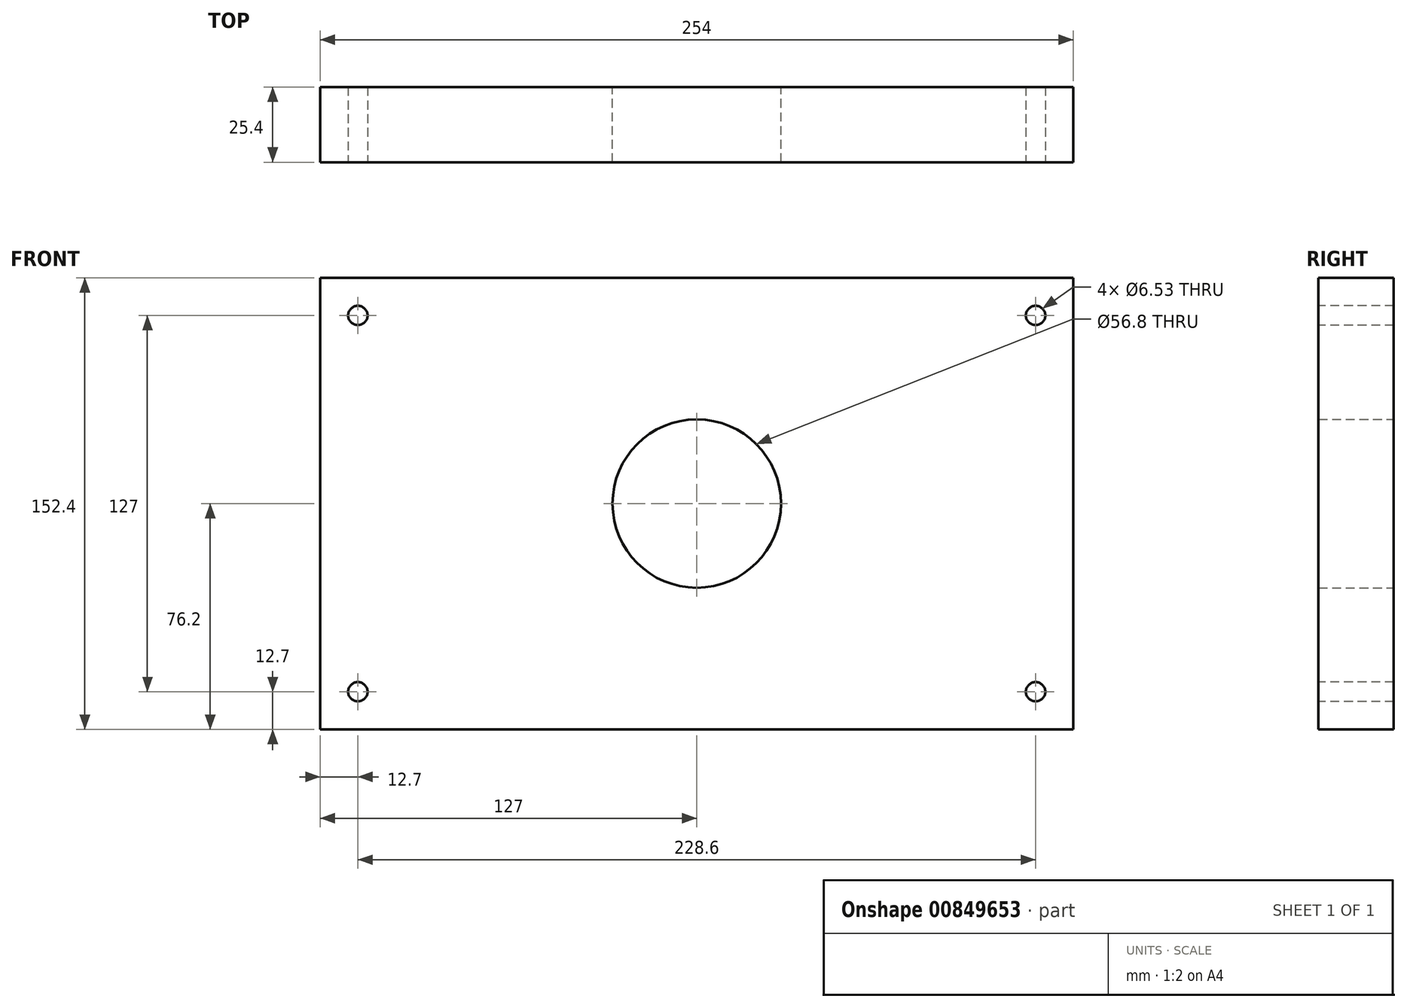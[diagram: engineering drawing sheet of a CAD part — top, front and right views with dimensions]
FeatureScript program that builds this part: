
annotation { "Feature Type Name" : "Feature", "Feature Type Description" : "" }
export const myFeature = defineFeature(function(context is Context, id is Id, definition is map)
    precondition{}
    {
        {
            var Q0;
            Q0=qCreatedBy(makeId("Front.planeOp"),FACE);
            var sketch = newSketch(context, id + "F0", { "sketchPlane" : qUnion([Q0])});
            skLineSegment(sketch, "E0", {"start": v(0, 0) * mm, "end": v(254, 0) * mm});
            skLineSegment(sketch, "E1", {"start": v(254, 0) * mm, "end": v(254, 152.4) * mm});
            skLineSegment(sketch, "E2", {"start": v(254, 152.4) * mm, "end": v(0, 152.4) * mm});
            skLineSegment(sketch, "E3", {"start": v(0, 152.4) * mm, "end": v(0, 0) * mm});
            skSolve(sketch);
        }
        {
            var Q0;
            Q0=makeQuery(id+"F0.imprint","IMPRINT",FACE,{"disambiguationData":[TD([[makeQuery(id+"F0.imprint","IMPRINT",EDGE,{"derivedFrom":sQuery(id+"F0.wireOp",EDGE,"E0")}),1.0]])]});
            extrude(context, id + "F1", {"entities" : qUnion([Q0]), "depth" : 25.4 * mm, "offsetDistance" : 25.4 * mm});
        }
        {
            var Q0;
            Q0=makeQuery(id+"F1.opExtrude","CAP_FACE",FACE,{"disambiguationData":[OSD([sQuery(id+"F0.wireOp",EDGE,"E0"),sQuery(id+"F0.wireOp",EDGE,"E1"),sQuery(id+"F0.wireOp",EDGE,"E2"),sQuery(id+"F0.wireOp",EDGE,"E3")])],"isStart":false});
            var sketch = newSketch(context, id + "F2", { "sketchPlane" : qUnion([Q0])});
            skPoint(sketch, "E4", {"position": v(12.7, 139.7) * mm});
            skPoint(sketch, "E5", {"position": v(241.3, 139.7) * mm});
            skPoint(sketch, "E6", {"position": v(241.3, 12.7) * mm});
            skPoint(sketch, "E7", {"position": v(12.7, 12.7) * mm});
            skSolve(sketch);
        }
        {
            var Q0;
            Q0=sQuery(id+"F2.wireOp",VERTEX,"E4");
            var Q1;
            Q1=sQuery(id+"F2.wireOp",VERTEX,"E5");
            var Q2;
            Q2=sQuery(id+"F2.wireOp",VERTEX,"E6");
            var Q3;
            Q3=sQuery(id+"F2.wireOp",VERTEX,"E7");
            var Q4;
            Q4=makeQuery(id+"F1.opExtrude","SWEPT_BODY",BODY,{"disambiguationData":[OSD([sQuery(id+"F0.wireOp",EDGE,"E0"),sQuery(id+"F0.wireOp",EDGE,"E1"),sQuery(id+"F0.wireOp",EDGE,"E2"),sQuery(id+"F0.wireOp",EDGE,"E3")])]});
            hole(context, id + "F3", {"style" : HoleStyle.SIMPLE, "endStyle" : HoleEndStyle.THROUGH, "standardTappedOrClearance" : lookupTablePath({ "fit" : "Close", "standard" : "ANSI", "size" : "1/4", "type" : "Clearance" }), "standardBlindInLast" : lookupTablePath({ "fit" : "Close", "standard" : "ANSI", "size" : "1/4", "type" : "Clearance" }), "holeDiameter" : 6.53 * mm, "majorDiameter" : 6.35 * mm, "isTappedThrough" : true, "tappedDepth" : 12.7 * mm, "tapClearance" : 3, "locations" : qUnion([Q0, Q1, Q2, Q3]), "scope" : qUnion([Q4])});
        }
        {
            var Q0;
            Q0=makeQuery(id+"F1.opExtrude","CAP_FACE",FACE,{"disambiguationData":[OSD([sQuery(id+"F0.wireOp",EDGE,"E0"),sQuery(id+"F0.wireOp",EDGE,"E1"),sQuery(id+"F0.wireOp",EDGE,"E2"),sQuery(id+"F0.wireOp",EDGE,"E3")])],"isStart":true});
            var sketch = newSketch(context, id + "F4", { "sketchPlane" : qUnion([Q0])});
            skCircle(sketch, "E8", {"center": v(-127, 76.2) * mm, "radius": 28.4 * mm});
            skSolve(sketch);
        }
        {
            var Q0;
            Q0=makeQuery(id+"F4.imprint","IMPRINT",FACE,{"disambiguationData":[TD([[makeQuery(id+"F4.imprint","IMPRINT",EDGE,{"derivedFrom":sQuery(id+"F4.wireOp",EDGE,"E8")}),1.0]])]});
            extrude(context, id + "F5", {"entities" : qUnion([Q0]), "operationType" : NewBodyOperationType.REMOVE, "endBound" : BoundingType.THROUGH_ALL, "oppositeDirection" : true, "depth" : 25.4 * mm, "offsetDistance" : 25.4 * mm});
        }
    });
